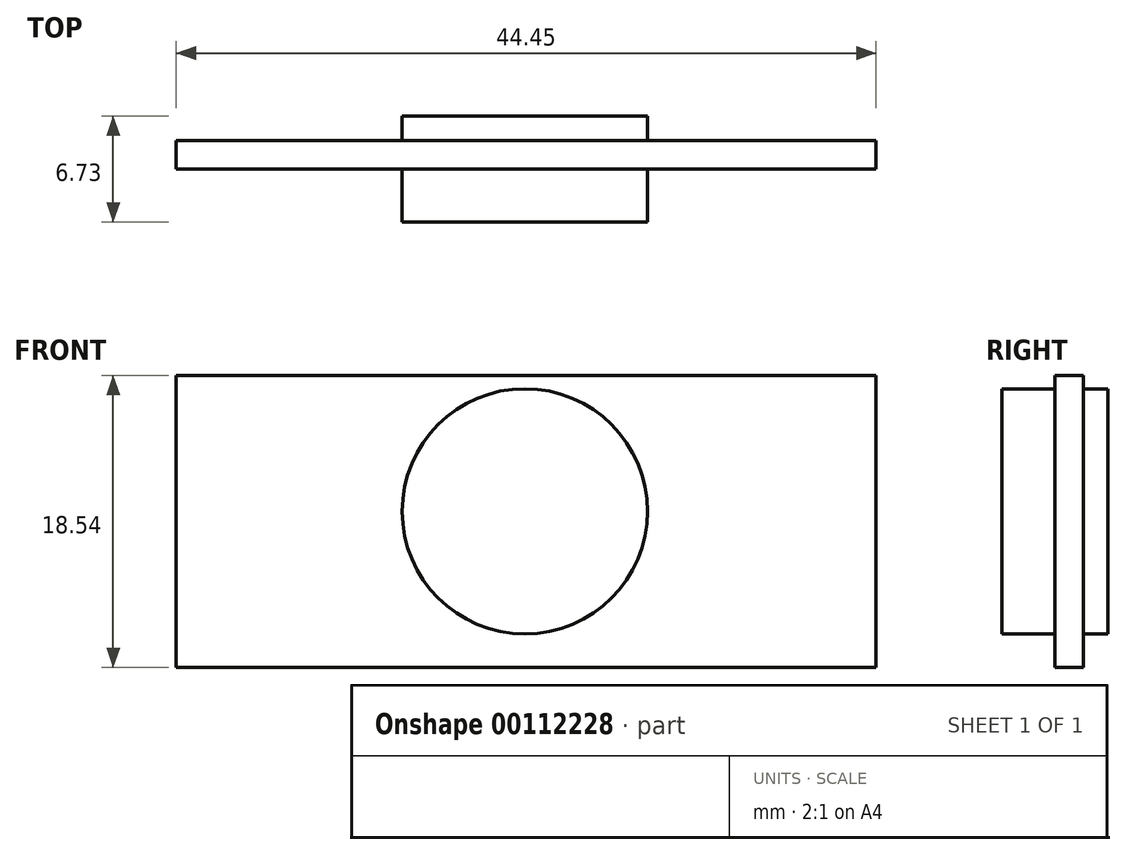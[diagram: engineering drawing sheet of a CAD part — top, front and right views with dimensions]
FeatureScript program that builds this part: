
annotation { "Feature Type Name" : "Feature", "Feature Type Description" : "" }
export const myFeature = defineFeature(function(context is Context, id is Id, definition is map)
    precondition{}
    {
        {
            var Q0;
            Q0=qCreatedBy(makeId("Front.planeOp"),FACE);
            var sketch = newSketch(context, id + "F0", { "sketchPlane" : qUnion([Q0])});
            skLineSegment(sketch, "E0.bottom", {"start": v(-26.38, -10.38) * mm, "end": v(18.07, -10.38) * mm});
            skLineSegment(sketch, "E0.top", {"start": v(-26.38, 8.16) * mm, "end": v(18.07, 8.16) * mm});
            skLineSegment(sketch, "E0.left", {"start": v(-26.38, -10.38) * mm, "end": v(-26.38, 8.16) * mm});
            skLineSegment(sketch, "E0.right", {"start": v(18.07, -10.38) * mm, "end": v(18.07, 8.16) * mm});
            skSolve(sketch);
        }
        {
            var Q0;
            Q0=makeQuery(id+"F0.imprint","IMPRINT",FACE,{"disambiguationData":[TD([[makeQuery(id+"F0.imprint","IMPRINT",EDGE,{"derivedFrom":sQuery(id+"F0.wireOp",EDGE,"E0.bottom")}),1.0]])]});
            extrude(context, id + "F1", {"entities" : qUnion([Q0]), "depth" : 1.8 * mm});
        }
        {
            var Q0;
            Q0=makeQuery(id+"F1.opExtrude","CAP_FACE",FACE,{"disambiguationData":[OSD([sQuery(id+"F0.wireOp",EDGE,"E0.bottom"),sQuery(id+"F0.wireOp",EDGE,"E0.top"),sQuery(id+"F0.wireOp",EDGE,"E0.left"),sQuery(id+"F0.wireOp",EDGE,"E0.right")])],"isStart":false});
            var sketch = newSketch(context, id + "F2", { "sketchPlane" : qUnion([Q0])});
            skCircle(sketch, "E1", {"center": v(-4.24, -0.46) * mm, "radius": 7.79 * mm});
            skSolve(sketch);
        }
        {
            var Q0;
            Q0=makeQuery(id+"F2.imprint","IMPRINT",FACE,{"disambiguationData":[TD([[makeQuery(id+"F2.imprint","IMPRINT",EDGE,{"derivedFrom":sQuery(id+"F2.wireOp",EDGE,"E1")}),1.0]])]});
            extrude(context, id + "F3", {"entities" : qUnion([Q0]), "operationType" : NewBodyOperationType.ADD, "endBound" : BoundingType.SYMMETRIC, "depth" : 6.73 * mm});
        }
    });
